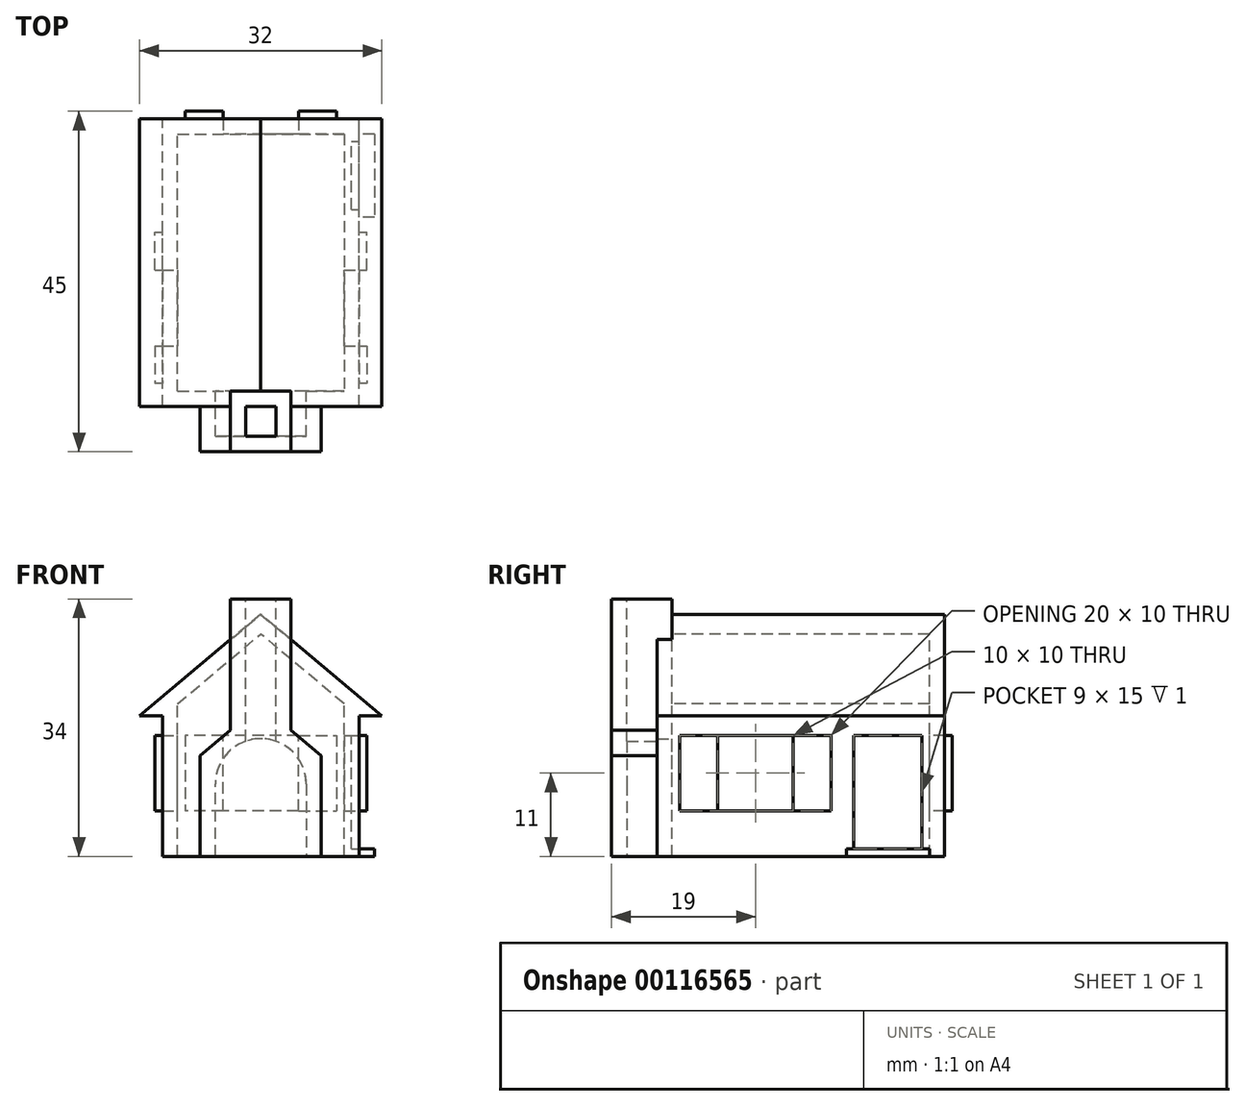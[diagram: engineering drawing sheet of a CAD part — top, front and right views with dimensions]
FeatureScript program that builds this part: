
annotation { "Feature Type Name" : "Feature", "Feature Type Description" : "" }
export const myFeature = defineFeature(function(context is Context, id is Id, definition is map)
    precondition{}
    {
        {
            var Q0;
            Q0=qCreatedBy(makeId("Front.planeOp"),FACE);
            var sketch = newSketch(context, id + "F0", { "sketchPlane" : qUnion([Q0])});
            skLineSegment(sketch, "E0", {"start": v(-13, 0) * mm, "end": v(13, 0) * mm});
            skLineSegment(sketch, "E1", {"start": v(13, 0) * mm, "end": v(13, 18.57) * mm});
            skLineSegment(sketch, "E2", {"start": v(13, 18.57) * mm, "end": v(16, 18.57) * mm});
            skLineSegment(sketch, "E3", {"start": v(16, 18.57) * mm, "end": v(0, 32) * mm});
            skLineSegment(sketch, "E4.MirrorCS", {"start": v(-16, 18.57) * mm, "end": v(0, 32) * mm});
            skLineSegment(sketch, "E5.MirrorCS", {"start": v(-13, 18.57) * mm, "end": v(-16, 18.57) * mm});
            skLineSegment(sketch, "E6.MirrorCS", {"start": v(-13, 0) * mm, "end": v(-13, 18.57) * mm});
            skSolve(sketch);
        }
        {
            var Q0;
            Q0 = qSketchRegion(id + "F0", true);
            extrude(context, id + "F1", {"entities" : qUnion([Q0]), "endBound" : BoundingType.SYMMETRIC, "depth" : 38 * mm});
        }
        {
            var Q0;
            Q0=qCreatedBy(makeId("Front.planeOp"),FACE);
            var sketch = newSketch(context, id + "F2", { "sketchPlane" : qUnion([Q0])});
            skLineSegment(sketch, "E7.bottom", {"start": v(-5, 16) * mm, "end": v(5, 16) * mm});
            skLineSegment(sketch, "E7.top", {"start": v(-5, 6) * mm, "end": v(5, 6) * mm});
            skLineSegment(sketch, "E7.left", {"start": v(-5, 16) * mm, "end": v(-5, 6) * mm});
            skLineSegment(sketch, "E7.right", {"start": v(5, 16) * mm, "end": v(5, 6) * mm});
            skSolve(sketch);
        }
        {
            var Q0;
            Q0 = qSketchRegion(id + "F2", true);
            extrude(context, id + "F3", {"entities" : qUnion([Q0]), "operationType" : NewBodyOperationType.REMOVE, "endBound" : BoundingType.THROUGH_ALL, "oppositeDirection" : true, "depth" : 25.4 * mm});
        }
        {
            var Q0;
            Q0=makeQuery(id+"F3.boolean.opBoolean","COPY",FACE,{"derivedFrom":makeQuery(id+"F3.opExtrude","SWEPT_FACE",FACE,{"disambiguationData":[OSD([sQuery(id+"F2.wireOp",EDGE,"E7.top")])]})});
            var sketch = newSketch(context, id + "F4", { "sketchPlane" : qUnion([Q0])});
            skLineSegment(sketch, "E8.bottom", {"start": v(-14, -16) * mm, "end": v(14, -16) * mm});
            skLineSegment(sketch, "E8.top", {"start": v(-14, 4) * mm, "end": v(14, 4) * mm});
            skLineSegment(sketch, "E8.left", {"start": v(-14, -16) * mm, "end": v(-14, 4) * mm});
            skLineSegment(sketch, "E8.right", {"start": v(14, -16) * mm, "end": v(14, 4) * mm});
            skSolve(sketch);
        }
        {
            var Q0;
            Q0 = qSketchRegion(id + "F4", true);
            var Q1;
            Q1=makeQuery(id+"F3.boolean.opBoolean","COPY",FACE,{"derivedFrom":makeQuery(id+"F3.opExtrude","SWEPT_FACE",FACE,{"disambiguationData":[OSD([sQuery(id+"F2.wireOp",EDGE,"E7.bottom")])]})});
            extrude(context, id + "F5", {"entities" : qUnion([Q0]), "operationType" : NewBodyOperationType.ADD, "endBound" : BoundingType.UP_TO_SURFACE, "endBoundEntityFace" : qUnion([Q1]), "depth" : 25.4 * mm});
        }
        {
            var Q0;
            Q0=qCreatedBy(makeId("Right.planeOp"),FACE);
            var sketch = newSketch(context, id + "F6", { "sketchPlane" : qUnion([Q0])});
            skLineSegment(sketch, "E9.bottom", {"start": v(-11, 16) * mm, "end": v(-1, 16) * mm});
            skLineSegment(sketch, "E9.top", {"start": v(-11, 6) * mm, "end": v(-1, 6) * mm});
            skLineSegment(sketch, "E9.left", {"start": v(-11, 16) * mm, "end": v(-11, 6) * mm});
            skLineSegment(sketch, "E9.right", {"start": v(-1, 16) * mm, "end": v(-1, 6) * mm});
            skSolve(sketch);
        }
        {
            var Q0;
            Q0 = qSketchRegion(id + "F6", true);
            extrude(context, id + "F7", {"entities" : qUnion([Q0]), "operationType" : NewBodyOperationType.REMOVE, "endBound" : BoundingType.THROUGH_ALL, "oppositeDirection" : true, "depth" : 25.4 * mm, "hasSecondDirection" : true, "secondDirectionBound" : SecondDirectionBoundingType.THROUGH_ALL, "secondDirectionOppositeDirection" : false, "secondDirectionDepth" : 25.4 * mm});
        }
        {
            var Q0;
            Q0=makeQuery(id+"F1.opExtrude","CAP_FACE",FACE,{"disambiguationData":[OSD([sQuery(id+"F0.wireOp",EDGE,"E0"),sQuery(id+"F0.wireOp",EDGE,"E2"),sQuery(id+"F0.wireOp",EDGE,"E3"),sQuery(id+"F0.wireOp",EDGE,"E4.MirrorCS"),sQuery(id+"F0.wireOp",EDGE,"E5.MirrorCS"),sQuery(id+"F0.wireOp",EDGE,"E6.MirrorCS"),sQuery(id+"F0.wireOp",EDGE,"E1")])],"isStart":true});
            var sketch = newSketch(context, id + "F8", { "sketchPlane" : qUnion([Q0])});
            skLineSegment(sketch, "E10.bottom", {"start": v(-5, 16) * mm, "end": v(-10, 16) * mm});
            skLineSegment(sketch, "E10.top", {"start": v(-5, 6) * mm, "end": v(-10, 6) * mm});
            skLineSegment(sketch, "E10.left", {"start": v(-5, 16) * mm, "end": v(-5, 6) * mm});
            skLineSegment(sketch, "E10.right", {"start": v(-10, 16) * mm, "end": v(-10, 6) * mm});
            skLineSegment(sketch, "E11.bottom", {"start": v(5, 16) * mm, "end": v(10, 16) * mm});
            skLineSegment(sketch, "E11.top", {"start": v(5, 6) * mm, "end": v(10, 6) * mm});
            skLineSegment(sketch, "E11.left", {"start": v(5, 16) * mm, "end": v(5, 6) * mm});
            skLineSegment(sketch, "E11.right", {"start": v(10, 16) * mm, "end": v(10, 6) * mm});
            skSolve(sketch);
        }
        {
            var Q0;
            Q0 = qSketchRegion(id + "F8", true);
            extrude(context, id + "F9", {"entities" : qUnion([Q0]), "operationType" : NewBodyOperationType.ADD, "depth" : 1 * mm});
        }
        {
            var Q0;
            Q0=makeQuery(id+"F1.opExtrude","SWEPT_FACE",FACE,{"disambiguationData":[OSD([sQuery(id+"F0.wireOp",EDGE,"E2")])]});
            var sketch = newSketch(context, id + "F10", { "sketchPlane" : qUnion([Q0])});
            skLineSegment(sketch, "E12.bottom", {"start": v(-11, 17) * mm, "end": v(11, 17) * mm});
            skLineSegment(sketch, "E12.left", {"start": v(-11, 17) * mm, "end": v(-11, -17) * mm});
            skLineSegment(sketch, "E13", {"start": v(11, -17) * mm, "end": v(11, 17) * mm});
            skLineSegment(sketch, "E14", {"start": v(-11, -17) * mm, "end": v(11, -17) * mm});
            skSolve(sketch);
        }
        {
            var Q0;
            Q0 = qSketchRegion(id + "F10", true);
            var Q1;
            Q1=makeQuery(id+"F1.opExtrude","SWEPT_FACE",FACE,{"disambiguationData":[OSD([sQuery(id+"F0.wireOp",EDGE,"E0")])]});
            extrude(context, id + "F11", {"entities" : qUnion([Q0]), "operationType" : NewBodyOperationType.REMOVE, "endBound" : BoundingType.THROUGH_ALL, "endBoundEntityFace" : qUnion([Q1]), "depth" : 25.4 * mm});
        }
        {
            var Q0;
            Q0=qCreatedBy(makeId("Front.planeOp"),FACE);
            var sketch = newSketch(context, id + "F12", { "sketchPlane" : qUnion([Q0])});
            skLineSegment(sketch, "E15", {"start": v(-11, 18.57) * mm, "end": v(11, 18.57) * mm});
            skLineSegment(sketch, "E16", {"start": v(0, 29.39) * mm, "end": v(-11, 20.16) * mm});
            skLineSegment(sketch, "E17", {"start": v(-11, 20.16) * mm, "end": v(-11, 18.57) * mm});
            skLineSegment(sketch, "E18", {"start": v(0, 29.39) * mm, "end": v(11, 20.16) * mm});
            skLineSegment(sketch, "E19", {"start": v(11, 20.16) * mm, "end": v(11, 18.57) * mm});
            skSolve(sketch);
        }
        {
            var Q0;
            Q0 = qSketchRegion(id + "F12", true);
            var Q1;
            Q1=makeQuery(id+"F11.boolean.opBoolean","COPY",FACE,{"derivedFrom":makeQuery(id+"F11.opExtrude","SWEPT_FACE",FACE,{"disambiguationData":[OSD([sQuery(id+"F10.wireOp",EDGE,"E14")])]})});
            var Q2;
            Q2=makeQuery(id+"F11.boolean.opBoolean","COPY",FACE,{"derivedFrom":makeQuery(id+"F11.opExtrude","SWEPT_FACE",FACE,{"disambiguationData":[OSD([sQuery(id+"F10.wireOp",EDGE,"E12.bottom")])]})});
            extrude(context, id + "F13", {"entities" : qUnion([Q0]), "operationType" : NewBodyOperationType.REMOVE, "endBound" : BoundingType.UP_TO_SURFACE, "oppositeDirection" : true, "endBoundEntityFace" : qUnion([Q1]), "depth" : 25.4 * mm, "hasSecondDirection" : true, "secondDirectionBound" : SecondDirectionBoundingType.UP_TO_SURFACE, "secondDirectionOppositeDirection" : false, "secondDirectionBoundEntityFace" : qUnion([Q2]), "secondDirectionDepth" : 25.4 * mm});
        }
        {
            var Q0;
            Q0=qCreatedBy(makeId("Top.planeOp"),FACE);
            var sketch = newSketch(context, id + "F14", { "sketchPlane" : qUnion([Q0])});
            skLineSegment(sketch, "E20.bottom", {"start": v(-4, -17) * mm, "end": v(4, -17) * mm});
            skLineSegment(sketch, "E20.top", {"start": v(-4, -25) * mm, "end": v(4, -25) * mm});
            skLineSegment(sketch, "E20.left", {"start": v(-4, -17) * mm, "end": v(-4, -25) * mm});
            skLineSegment(sketch, "E20.right", {"start": v(4, -17) * mm, "end": v(4, -25) * mm});
            skSolve(sketch);
        }
        {
            var Q0;
            Q0 = qSketchRegion(id + "F14", true);
            extrude(context, id + "F15", {"entities" : qUnion([Q0]), "operationType" : NewBodyOperationType.ADD, "depth" : 34 * mm});
        }
        {
            var Q0;
            Q0=makeQuery(id+"F15.opExtrude","SWEPT_FACE",FACE,{"disambiguationData":[OSD([sQuery(id+"F14.wireOp",EDGE,"E20.top")])]});
            var sketch = newSketch(context, id + "F16", { "sketchPlane" : qUnion([Q0])});
            skLineSegment(sketch, "E21", {"start": v(0, 20) * mm, "end": v(-8, 13.29) * mm});
            skLineSegment(sketch, "E22", {"start": v(-8, 13.29) * mm, "end": v(-8, 0) * mm});
            skLineSegment(sketch, "E23", {"start": v(-8, 0) * mm, "end": v(8, 0) * mm});
            skLineSegment(sketch, "E24", {"start": v(8, 0) * mm, "end": v(8, 13.29) * mm});
            skLineSegment(sketch, "E25", {"start": v(8, 13.29) * mm, "end": v(0, 20) * mm});
            skSolve(sketch);
        }
        {
            var Q0;
            Q0 = qSketchRegion(id + "F16", true);
            var Q1;
            {var subQ0=sQuery(id+"F10.wireOp",EDGE,"E12.bottom");Q1=makeQuery(id+"F13.boolean.opBoolean","MERGE",FACE,{"derivedFrom":[makeQuery(id+"F11.boolean.opBoolean","COPY",FACE,{"derivedFrom":makeQuery(id+"F11.opExtrude","SWEPT_FACE",FACE,{"disambiguationData":[OSD([subQ0])]})}),makeQuery(id+"F13.opExtrude","CAP_FACE",FACE,{"disambiguationData":[OSD([subQ0])],"isStart":true})]});}
            extrude(context, id + "F17", {"entities" : qUnion([Q0]), "operationType" : NewBodyOperationType.ADD, "endBound" : BoundingType.UP_TO_SURFACE, "oppositeDirection" : true, "endBoundEntityFace" : qUnion([Q1]), "depth" : 25.4 * mm});
        }
        {
            var Q0;
            Q0=makeQuery(id+"F15.opExtrude","CAP_FACE",FACE,{"disambiguationData":[OSD([sQuery(id+"F14.wireOp",EDGE,"E20.bottom"),sQuery(id+"F14.wireOp",EDGE,"E20.top"),sQuery(id+"F14.wireOp",EDGE,"E20.left"),sQuery(id+"F14.wireOp",EDGE,"E20.right")])],"isStart":false});
            var sketch = newSketch(context, id + "F18", { "sketchPlane" : qUnion([Q0])});
            skLineSegment(sketch, "E26.bottom", {"start": v(-2, -23) * mm, "end": v(2, -23) * mm});
            skLineSegment(sketch, "E26.top", {"start": v(-2, -19) * mm, "end": v(2, -19) * mm});
            skLineSegment(sketch, "E26.left", {"start": v(-2, -23) * mm, "end": v(-2, -19) * mm});
            skLineSegment(sketch, "E26.right", {"start": v(2, -23) * mm, "end": v(2, -19) * mm});
            skSolve(sketch);
        }
        {
            var Q0;
            Q0 = qSketchRegion(id + "F18", true);
            extrude(context, id + "F19", {"entities" : qUnion([Q0]), "operationType" : NewBodyOperationType.REMOVE, "endBound" : BoundingType.THROUGH_ALL, "oppositeDirection" : true, "depth" : 25.4 * mm});
        }
        {
            var Q0;
            Q0=qCreatedBy(makeId("Front.planeOp"),FACE);
            var sketch = newSketch(context, id + "F20", { "sketchPlane" : qUnion([Q0])});
            skLineSegment(sketch, "E27", {"start": v(-6, 9.56) * mm, "end": v(-6, 0) * mm});
            skLineSegment(sketch, "E28", {"start": v(-6, 0) * mm, "end": v(6, 0) * mm});
            skLineSegment(sketch, "E29", {"start": v(6, 0) * mm, "end": v(6, 9.56) * mm});
            skArc(sketch, "E30", {"start": v(6, 9.56) * mm, "mid": v(0, 15.56) * mm, "end": v(-6, 9.56) * mm});
            skSolve(sketch);
        }
        {
            var Q0;
            Q0=makeQuery(id+"F20.imprint","IMPRINT",FACE,{"disambiguationData":[TD([[makeQuery(id+"F20.imprint","IMPRINT",EDGE,{"derivedFrom":sQuery(id+"F20.wireOp",EDGE,"E27")}),1.0]])]});
            var Q1;
            Q1=makeQuery(id+"F19.boolean.opBoolean","COPY",FACE,{"derivedFrom":makeQuery(id+"F19.opExtrude","SWEPT_FACE",FACE,{"disambiguationData":[OSD([sQuery(id+"F18.wireOp",EDGE,"E26.bottom")])]})});
            extrude(context, id + "F21", {"entities" : qUnion([Q0]), "operationType" : NewBodyOperationType.REMOVE, "endBound" : BoundingType.UP_TO_SURFACE, "endBoundEntityFace" : qUnion([Q1]), "depth" : 25.4 * mm});
        }
        {
            var Q0;
            Q0=makeQuery(id+"F1.opExtrude","SWEPT_FACE",FACE,{"disambiguationData":[OSD([sQuery(id+"F0.wireOp",EDGE,"E1")])]});
            var sketch = newSketch(context, id + "F22", { "sketchPlane" : qUnion([Q0])});
            skLineSegment(sketch, "E31.bottom", {"start": v(7, 0) * mm, "end": v(16, 0) * mm});
            skLineSegment(sketch, "E31.top", {"start": v(7, 16) * mm, "end": v(16, 16) * mm});
            skLineSegment(sketch, "E31.left", {"start": v(7, 0) * mm, "end": v(7, 16) * mm});
            skLineSegment(sketch, "E31.right", {"start": v(16, 0) * mm, "end": v(16, 16) * mm});
            skSolve(sketch);
        }
        {
            var Q0;
            Q0 = qSketchRegion(id + "F22", true);
            extrude(context, id + "F23", {"entities" : qUnion([Q0]), "operationType" : NewBodyOperationType.REMOVE, "oppositeDirection" : true, "depth" : 1 * mm});
        }
        {
            var Q0;
            Q0=makeQuery(id+"F13.boolean.opBoolean","MERGE",FACE,{"derivedFrom":[makeQuery(id+"F11.boolean.opBoolean","COPY",FACE,{"derivedFrom":makeQuery(id+"F11.opExtrude","SWEPT_FACE",FACE,{"disambiguationData":[OSD([sQuery(id+"F10.wireOp",EDGE,"E13")])]})}),makeQuery(id+"F13.opExtrude","SWEPT_FACE",FACE,{"disambiguationData":[OSD([sQuery(id+"F12.wireOp",EDGE,"E19")])]})]});
            var sketch = newSketch(context, id + "F24", { "sketchPlane" : qUnion([Q0])});
            skLineSegment(sketch, "E32.bottom", {"start": v(-6, 0) * mm, "end": v(-17, 0) * mm});
            skLineSegment(sketch, "E32.top", {"start": v(-6, 1) * mm, "end": v(-17, 1) * mm});
            skLineSegment(sketch, "E32.left", {"start": v(-6, 0) * mm, "end": v(-6, 1) * mm});
            skLineSegment(sketch, "E32.right", {"start": v(-17, 0) * mm, "end": v(-17, 1) * mm});
            skSolve(sketch);
        }
        {
            var Q0;
            Q0 = qSketchRegion(id + "F24", true);
            extrude(context, id + "F25", {"entities" : qUnion([Q0]), "operationType" : NewBodyOperationType.ADD, "oppositeDirection" : true, "depth" : 4 * mm});
        }
    });
